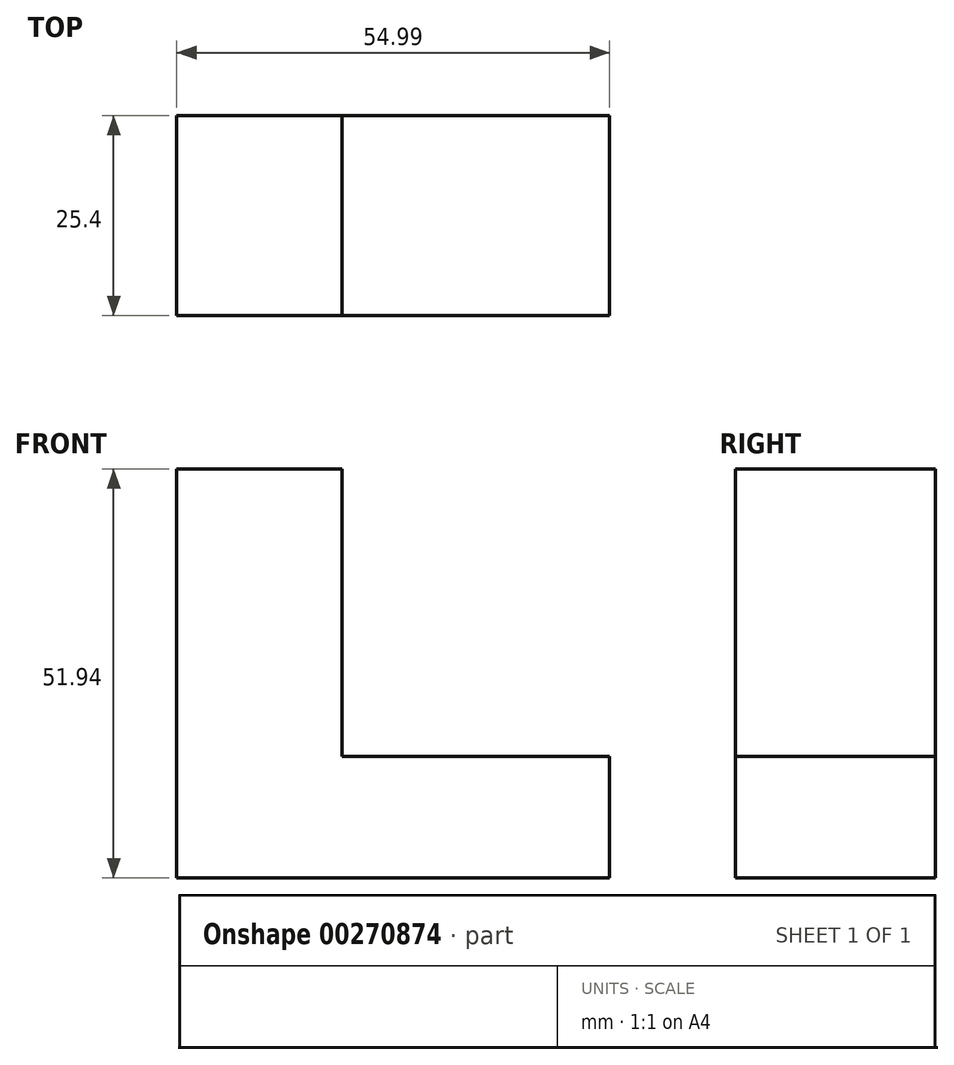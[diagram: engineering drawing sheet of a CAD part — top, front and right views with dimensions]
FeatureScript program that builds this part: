
annotation { "Feature Type Name" : "Feature", "Feature Type Description" : "" }
export const myFeature = defineFeature(function(context is Context, id is Id, definition is map)
    precondition{}
    {
        {
            var Q0;
            Q0=qCreatedBy(makeId("Front.planeOp"),FACE);
            var sketch = newSketch(context, id + "F0", { "sketchPlane" : qUnion([Q0])});
            skLineSegment(sketch, "E0.bottom", {"start": v(-55, 0) * mm, "end": v(0, 0) * mm});
            skLineSegment(sketch, "E0.top", {"start": v(-55, 0) * mm, "end": v(0, 0) * mm});
            skLineSegment(sketch, "E0.left", {"start": v(-55, 0) * mm, "end": v(-55, 0) * mm});
            skLineSegment(sketch, "E0.right", {"start": v(0, 0) * mm, "end": v(0, 0) * mm});
            skLineSegment(sketch, "E1.top", {"start": v(-55, 51.94) * mm, "end": v(-55, 51.94) * mm});
            skLineSegment(sketch, "E1.left", {"start": v(-55, 0) * mm, "end": v(-55, 51.94) * mm});
            skLineSegment(sketch, "E1.right", {"start": v(-55, 0) * mm, "end": v(-55, 51.94) * mm});
            skLineSegment(sketch, "E2.bottom", {"start": v(-33.99, 51.94) * mm, "end": v(-55, 51.94) * mm});
            skLineSegment(sketch, "E2.top", {"start": v(-33.99, 51.94) * mm, "end": v(-55, 51.94) * mm});
            skLineSegment(sketch, "E2.left", {"start": v(-33.99, 51.94) * mm, "end": v(-33.99, 51.94) * mm});
            skLineSegment(sketch, "E3.top", {"start": v(-33.99, 15.47) * mm, "end": v(-33.99, 15.47) * mm});
            skLineSegment(sketch, "E3.left", {"start": v(-33.99, 51.94) * mm, "end": v(-33.99, 15.47) * mm});
            skLineSegment(sketch, "E3.right", {"start": v(-33.99, 51.94) * mm, "end": v(-33.99, 15.47) * mm});
            skLineSegment(sketch, "E4.bottom", {"start": v(0, 15.47) * mm, "end": v(-33.99, 15.47) * mm});
            skLineSegment(sketch, "E4.top", {"start": v(0, 15.47) * mm, "end": v(-33.99, 15.47) * mm});
            skLineSegment(sketch, "E4.left", {"start": v(0, 15.47) * mm, "end": v(0, 15.47) * mm});
            skLineSegment(sketch, "E5.left", {"start": v(0, 0) * mm, "end": v(0, 15.47) * mm});
            skLineSegment(sketch, "E5.right", {"start": v(0, 0) * mm, "end": v(0, 15.47) * mm});
            skSolve(sketch);
        }
        {
            var Q0;
            Q0 = qSketchRegion(id + "F0", true);
            extrude(context, id + "F1", {"entities" : qUnion([Q0]), "depth" : 25.4 * mm});
        }
    });
